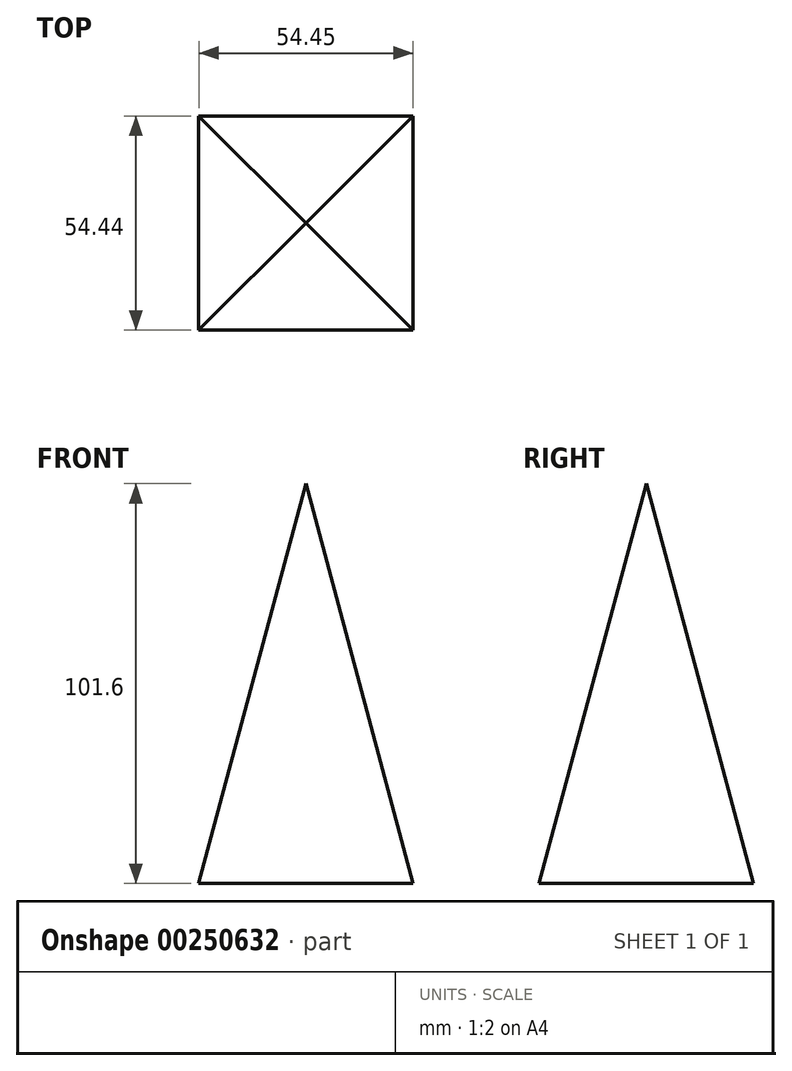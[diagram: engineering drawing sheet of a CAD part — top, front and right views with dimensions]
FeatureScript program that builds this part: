
annotation { "Feature Type Name" : "Feature", "Feature Type Description" : "" }
export const myFeature = defineFeature(function(context is Context, id is Id, definition is map)
    precondition{}
    {
        {
            var Q0;
            Q0=qCreatedBy(makeId("Top.planeOp"),FACE);
            var sketch = newSketch(context, id + "F0", { "sketchPlane" : qUnion([Q0])});
            skLineSegment(sketch, "E0.bottom", {"start": v(-45.07, 43.32) * mm, "end": v(43.83, 43.32) * mm});
            skLineSegment(sketch, "E0.top", {"start": v(-45.07, -45.58) * mm, "end": v(43.83, -45.58) * mm});
            skLineSegment(sketch, "E0.left", {"start": v(-45.07, 43.32) * mm, "end": v(-45.07, -45.58) * mm});
            skLineSegment(sketch, "E0.right", {"start": v(43.83, 43.32) * mm, "end": v(43.83, -45.58) * mm});
            skSolve(sketch);
        }
        {
            var Q0;
            Q0 = qSketchRegion(id + "F0", true);
            extrude(context, id + "F1", {"entities" : qUnion([Q0]), "depth" : 101.6 * mm});
        }
        {
            var Q0;
            Q0=makeQuery(id+"F1.opExtrude","CAP_EDGE",EDGE,{"disambiguationData":[OSD([sQuery(id+"F0.wireOp",EDGE,"E0.top")])],"isStart":false});
            var Q1;
            Q1=makeQuery(id+"F1.opExtrude","CAP_EDGE",EDGE,{"disambiguationData":[OSD([sQuery(id+"F0.wireOp",EDGE,"E0.bottom")])],"isStart":false});
            var Q2;
            Q2=makeQuery(id+"F1.opExtrude","CAP_EDGE",EDGE,{"disambiguationData":[OSD([sQuery(id+"F0.wireOp",EDGE,"E0.left")])],"isStart":false});
            var Q3;
            Q3=makeQuery(id+"F1.opExtrude","CAP_EDGE",EDGE,{"disambiguationData":[OSD([sQuery(id+"F0.wireOp",EDGE,"E0.right")])],"isStart":false});
            chamfer(context, id + "F2", {"entities" : qUnion([Q0, Q1, Q2, Q3]), "chamferType" : ChamferType.OFFSET_ANGLE, "width" : 44.45 * mm, "oppositeDirection" : false, "angle" : 75 * degree, "tangentPropagation" : true});
        }
    });
